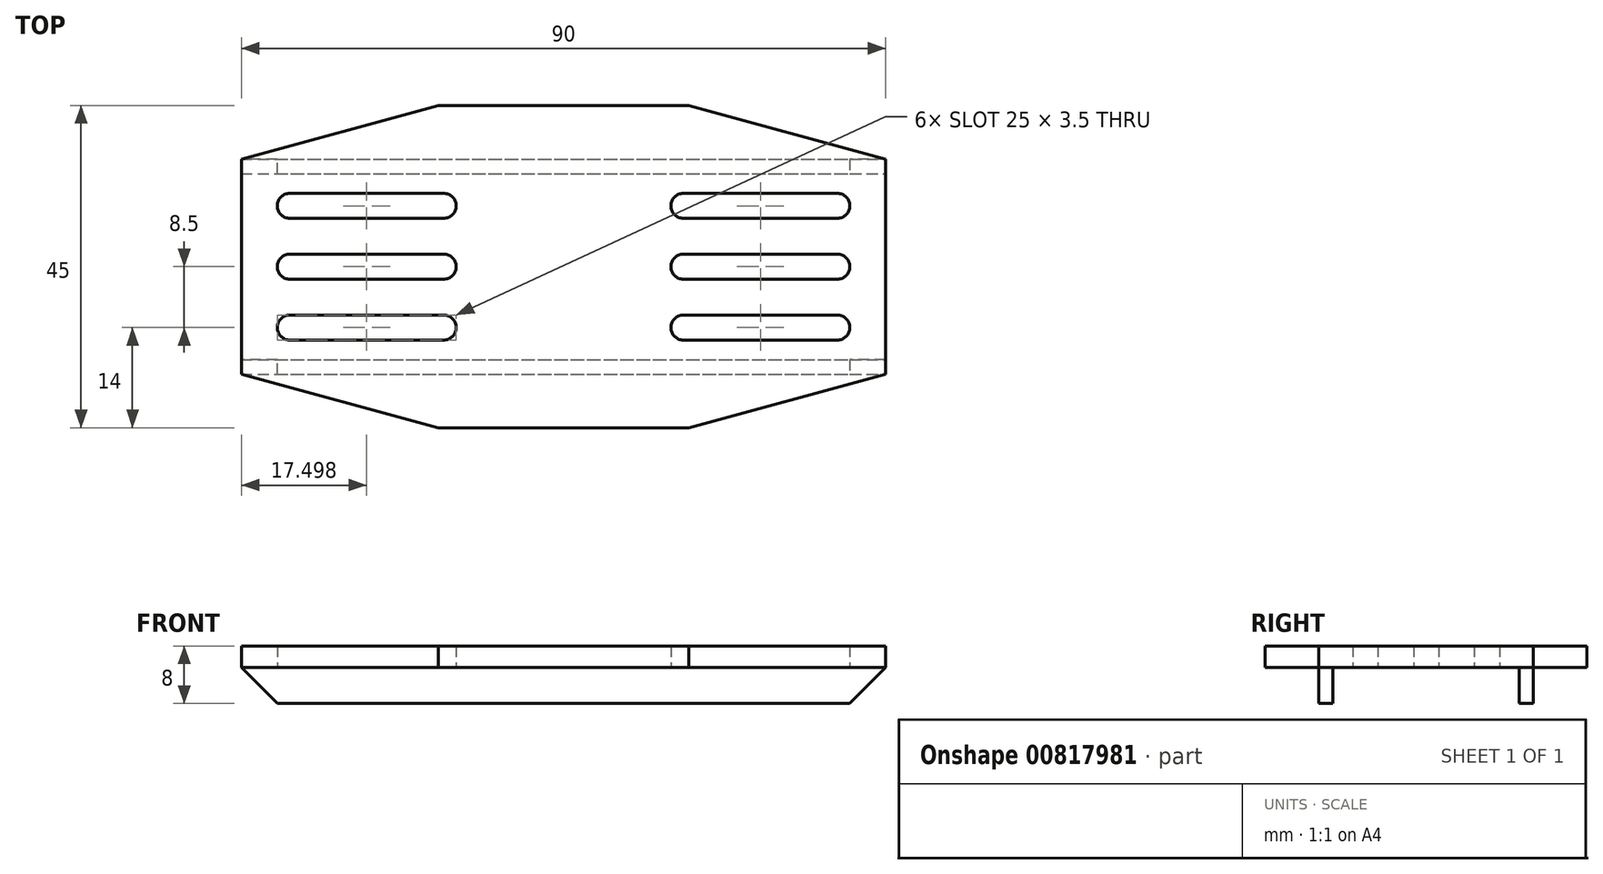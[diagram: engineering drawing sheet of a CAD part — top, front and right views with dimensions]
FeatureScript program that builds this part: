
annotation { "Feature Type Name" : "Feature", "Feature Type Description" : "" }
export const myFeature = defineFeature(function(context is Context, id is Id, definition is map)
    precondition{}
    {
        {
            var Q0;
            Q0=qCreatedBy(makeId("Top.planeOp"),FACE);
            var sketch = newSketch(context, id + "F0", { "sketchPlane" : qUnion([Q0])});
            skLineSegment(sketch, "E0", {"start": v(-65.37, 45) * mm, "end": v(-30.37, 45) * mm});
            skLineSegment(sketch, "E1", {"start": v(-30.37, 45) * mm, "end": v(-2.87, 37.5) * mm});
            skLineSegment(sketch, "E2", {"start": v(-2.87, 37.5) * mm, "end": v(-2.87, 7.5) * mm});
            skLineSegment(sketch, "E3", {"start": v(-2.87, 7.5) * mm, "end": v(-30.37, 0) * mm});
            skLineSegment(sketch, "E4", {"start": v(-30.37, 0) * mm, "end": v(-65.37, 0) * mm});
            skLineSegment(sketch, "E5", {"start": v(-65.37, 0) * mm, "end": v(-92.87, 7.5) * mm});
            skLineSegment(sketch, "E6", {"start": v(-92.87, 7.5) * mm, "end": v(-92.87, 37.5) * mm});
            skLineSegment(sketch, "E7", {"start": v(-92.87, 37.5) * mm, "end": v(-65.37, 45) * mm});
            skLineSegment(sketch, "E8", {"start": v(-92.87, 22.5) * mm, "end": v(-2.87, 22.5) * mm});
            skLineSegment(sketch, "E9", {"start": v(-92.87, 31) * mm, "end": v(-2.87, 31) * mm});
            skLineSegment(sketch, "E10", {"start": v(-92.87, 14) * mm, "end": v(-2.87, 14) * mm});
            skLineSegment(sketch, "E11.bottom", {"start": v(-86.12, 32.75) * mm, "end": v(-64.62, 32.75) * mm});
            skLineSegment(sketch, "E11.top", {"start": v(-86.12, 29.25) * mm, "end": v(-64.62, 29.25) * mm});
            skLineSegment(sketch, "E11.left", {"start": v(-87.87, 31) * mm, "end": v(-87.87, 31) * mm});
            skLineSegment(sketch, "E11.right", {"start": v(-62.87, 31) * mm, "end": v(-62.87, 31) * mm});
            skLineSegment(sketch, "E12.bottom", {"start": v(-86.12, 15.75) * mm, "end": v(-64.62, 15.75) * mm});
            skLineSegment(sketch, "E12.top", {"start": v(-86.12, 12.25) * mm, "end": v(-64.62, 12.25) * mm});
            skLineSegment(sketch, "E12.left", {"start": v(-87.87, 14) * mm, "end": v(-87.87, 14) * mm});
            skLineSegment(sketch, "E12.right", {"start": v(-62.87, 14) * mm, "end": v(-62.87, 14) * mm});
            skLineSegment(sketch, "E13.bottom", {"start": v(-86.12, 24.25) * mm, "end": v(-64.62, 24.25) * mm});
            skLineSegment(sketch, "E13.top", {"start": v(-86.12, 20.75) * mm, "end": v(-64.62, 20.75) * mm});
            skLineSegment(sketch, "E13.left", {"start": v(-87.87, 22.5) * mm, "end": v(-87.87, 22.5) * mm});
            skLineSegment(sketch, "E13.right", {"start": v(-62.87, 22.5) * mm, "end": v(-62.87, 22.5) * mm});
            skLineSegment(sketch, "E14.bottom", {"start": v(-9.62, 32.75) * mm, "end": v(-31.12, 32.75) * mm});
            skLineSegment(sketch, "E14.top", {"start": v(-9.62, 29.25) * mm, "end": v(-31.12, 29.25) * mm});
            skLineSegment(sketch, "E14.left", {"start": v(-7.87, 31) * mm, "end": v(-7.87, 31) * mm});
            skLineSegment(sketch, "E14.right", {"start": v(-32.87, 31) * mm, "end": v(-32.87, 31) * mm});
            skLineSegment(sketch, "E15.bottom", {"start": v(-31.12, 24.25) * mm, "end": v(-9.62, 24.25) * mm});
            skLineSegment(sketch, "E15.top", {"start": v(-31.12, 20.75) * mm, "end": v(-9.62, 20.75) * mm});
            skLineSegment(sketch, "E15.left", {"start": v(-32.87, 22.5) * mm, "end": v(-32.87, 22.5) * mm});
            skLineSegment(sketch, "E15.right", {"start": v(-7.87, 22.5) * mm, "end": v(-7.87, 22.5) * mm});
            skLineSegment(sketch, "E16.bottom", {"start": v(-31.12, 15.75) * mm, "end": v(-9.62, 15.75) * mm});
            skLineSegment(sketch, "E16.top", {"start": v(-31.12, 12.25) * mm, "end": v(-9.62, 12.25) * mm});
            skLineSegment(sketch, "E16.left", {"start": v(-32.87, 14) * mm, "end": v(-32.87, 14) * mm});
            skLineSegment(sketch, "E16.right", {"start": v(-7.87, 14) * mm, "end": v(-7.87, 14) * mm});
            skLineSegment(sketch, "E17", {"start": v(-47.87, 45) * mm, "end": v(-47.87, 0) * mm});
            skLineSegment(sketch, "E18", {"start": v(-92.87, 37.5) * mm, "end": v(-2.87, 37.5) * mm});
            skLineSegment(sketch, "E19", {"start": v(-92.87, 7.5) * mm, "end": v(-2.87, 7.5) * mm});
            skLineSegment(sketch, "E20", {"start": v(-92.87, 9.5) * mm, "end": v(-2.87, 9.5) * mm});
            skLineSegment(sketch, "E21", {"start": v(-92.87, 35.5) * mm, "end": v(-2.87, 35.5) * mm});
            skPoint(sketch, "E22.visualSharp", {"position": v(-62.87, 32.75) * mm});
            skArc(sketch, "E22.filletArc", {"start": v(-62.87, 31) * mm, "mid": v(-63.38, 32.24) * mm, "end": v(-64.62, 32.75) * mm});
            skPoint(sketch, "E23.visualSharp", {"position": v(-62.87, 29.25) * mm});
            skArc(sketch, "E23.filletArc", {"start": v(-64.62, 29.25) * mm, "mid": v(-63.38, 29.76) * mm, "end": v(-62.87, 31) * mm});
            skPoint(sketch, "E24.visualSharp", {"position": v(-62.87, 24.25) * mm});
            skArc(sketch, "E24.filletArc", {"start": v(-62.87, 22.5) * mm, "mid": v(-63.38, 23.74) * mm, "end": v(-64.62, 24.25) * mm});
            skPoint(sketch, "E25.visualSharp", {"position": v(-62.87, 20.75) * mm});
            skArc(sketch, "E25.filletArc", {"start": v(-64.62, 20.75) * mm, "mid": v(-63.38, 21.26) * mm, "end": v(-62.87, 22.5) * mm});
            skPoint(sketch, "E26.visualSharp", {"position": v(-62.87, 15.75) * mm});
            skArc(sketch, "E26.filletArc", {"start": v(-62.87, 14) * mm, "mid": v(-63.38, 15.24) * mm, "end": v(-64.62, 15.75) * mm});
            skPoint(sketch, "E27.visualSharp", {"position": v(-62.87, 12.25) * mm});
            skArc(sketch, "E27.filletArc", {"start": v(-64.62, 12.25) * mm, "mid": v(-63.38, 12.76) * mm, "end": v(-62.87, 14) * mm});
            skPoint(sketch, "E28.visualSharp", {"position": v(-87.87, 12.25) * mm});
            skArc(sketch, "E28.filletArc", {"start": v(-87.87, 14) * mm, "mid": v(-87.36, 12.76) * mm, "end": v(-86.12, 12.25) * mm});
            skPoint(sketch, "E29.visualSharp", {"position": v(-87.87, 15.75) * mm});
            skArc(sketch, "E29.filletArc", {"start": v(-86.12, 15.75) * mm, "mid": v(-87.36, 15.24) * mm, "end": v(-87.87, 14) * mm});
            skPoint(sketch, "E30.visualSharp", {"position": v(-87.87, 20.75) * mm});
            skArc(sketch, "E30.filletArc", {"start": v(-87.87, 22.5) * mm, "mid": v(-87.36, 21.26) * mm, "end": v(-86.12, 20.75) * mm});
            skPoint(sketch, "E31.visualSharp", {"position": v(-87.87, 24.25) * mm});
            skArc(sketch, "E31.filletArc", {"start": v(-86.12, 24.25) * mm, "mid": v(-87.36, 23.74) * mm, "end": v(-87.87, 22.5) * mm});
            skPoint(sketch, "E32.visualSharp", {"position": v(-87.87, 32.75) * mm});
            skArc(sketch, "E32.filletArc", {"start": v(-86.12, 32.75) * mm, "mid": v(-87.36, 32.24) * mm, "end": v(-87.87, 31) * mm});
            skPoint(sketch, "E33.visualSharp", {"position": v(-87.87, 29.25) * mm});
            skArc(sketch, "E33.filletArc", {"start": v(-87.87, 31) * mm, "mid": v(-87.36, 29.76) * mm, "end": v(-86.12, 29.25) * mm});
            skPoint(sketch, "E34.visualSharp", {"position": v(-32.87, 32.75) * mm});
            skArc(sketch, "E34.filletArc", {"start": v(-31.12, 32.75) * mm, "mid": v(-32.36, 32.24) * mm, "end": v(-32.87, 31) * mm});
            skPoint(sketch, "E35.visualSharp", {"position": v(-32.87, 29.25) * mm});
            skArc(sketch, "E35.filletArc", {"start": v(-32.87, 31) * mm, "mid": v(-32.36, 29.76) * mm, "end": v(-31.12, 29.25) * mm});
            skPoint(sketch, "E36.visualSharp", {"position": v(-7.87, 32.75) * mm});
            skArc(sketch, "E36.filletArc", {"start": v(-7.87, 31) * mm, "mid": v(-8.38, 32.24) * mm, "end": v(-9.62, 32.75) * mm});
            skPoint(sketch, "E37.visualSharp", {"position": v(-7.87, 29.25) * mm});
            skArc(sketch, "E37.filletArc", {"start": v(-9.62, 29.25) * mm, "mid": v(-8.38, 29.76) * mm, "end": v(-7.87, 31) * mm});
            skPoint(sketch, "E38.visualSharp", {"position": v(-7.87, 24.25) * mm});
            skArc(sketch, "E38.filletArc", {"start": v(-7.87, 22.5) * mm, "mid": v(-8.38, 23.74) * mm, "end": v(-9.62, 24.25) * mm});
            skPoint(sketch, "E39.visualSharp", {"position": v(-7.87, 20.75) * mm});
            skArc(sketch, "E39.filletArc", {"start": v(-9.62, 20.75) * mm, "mid": v(-8.38, 21.26) * mm, "end": v(-7.87, 22.5) * mm});
            skPoint(sketch, "E40.visualSharp", {"position": v(-32.87, 20.75) * mm});
            skArc(sketch, "E40.filletArc", {"start": v(-32.87, 22.5) * mm, "mid": v(-32.36, 21.26) * mm, "end": v(-31.12, 20.75) * mm});
            skPoint(sketch, "E41.visualSharp", {"position": v(-32.87, 24.25) * mm});
            skArc(sketch, "E41.filletArc", {"start": v(-31.12, 24.25) * mm, "mid": v(-32.36, 23.74) * mm, "end": v(-32.87, 22.5) * mm});
            skPoint(sketch, "E42.visualSharp", {"position": v(-32.87, 15.75) * mm});
            skArc(sketch, "E42.filletArc", {"start": v(-31.12, 15.75) * mm, "mid": v(-32.36, 15.24) * mm, "end": v(-32.87, 14) * mm});
            skPoint(sketch, "E43.visualSharp", {"position": v(-32.87, 12.25) * mm});
            skArc(sketch, "E43.filletArc", {"start": v(-32.87, 14) * mm, "mid": v(-32.36, 12.76) * mm, "end": v(-31.12, 12.25) * mm});
            skPoint(sketch, "E44.visualSharp", {"position": v(-7.87, 15.75) * mm});
            skArc(sketch, "E44.filletArc", {"start": v(-7.87, 14) * mm, "mid": v(-8.38, 15.24) * mm, "end": v(-9.62, 15.75) * mm});
            skPoint(sketch, "E45.visualSharp", {"position": v(-7.87, 12.25) * mm});
            skArc(sketch, "E45.filletArc", {"start": v(-9.62, 12.25) * mm, "mid": v(-8.38, 12.76) * mm, "end": v(-7.87, 14) * mm});
            skSolve(sketch);
        }
        {
            var Q0;
            Q0 = qSketchRegion(id + "F0", true);
            extrude(context, id + "F1", {"entities" : qUnion([Q0]), "depth" : 3 * mm, "offsetDistance" : 25 * mm});
        }
        {
            var Q0;
            {var subQ0=sQuery(id+"F0.wireOp",EDGE,"E18");var subQ5=sQuery(id+"F0.wireOp",EDGE,"E17");var subQ6=makeQuery(id+"F0.imprint","INTERSECT",VERTEX,{"derivedFrom":[subQ5,subQ0]});Q0=makeQuery(id+"F0.imprint","IMPRINT",FACE,{"disambiguationData":[TD([[makeQuery(id+"F0.imprint","IMPRINT",EDGE,{"disambiguationData":[TD([[subQ6,-1.0]])],"derivedFrom":subQ5}),1.0]])]});}
            var Q1;
            {var subQ0=sQuery(id+"F0.wireOp",EDGE,"E18");var subQ5=sQuery(id+"F0.wireOp",EDGE,"E17");var subQ6=makeQuery(id+"F0.imprint","INTERSECT",VERTEX,{"derivedFrom":[subQ5,subQ0]});Q1=makeQuery(id+"F0.imprint","IMPRINT",FACE,{"disambiguationData":[TD([[makeQuery(id+"F0.imprint","IMPRINT",EDGE,{"disambiguationData":[TD([[subQ6,-1.0]])],"derivedFrom":subQ5}),-1.0]])]});}
            var Q2;
            {var subQ3=sQuery(id+"F0.wireOp",EDGE,"E20");var subQ5=sQuery(id+"F0.wireOp",EDGE,"E17");var subQ6=makeQuery(id+"F0.imprint","INTERSECT",VERTEX,{"derivedFrom":[subQ5,subQ3]});Q2=makeQuery(id+"F0.imprint","IMPRINT",FACE,{"disambiguationData":[TD([[makeQuery(id+"F0.imprint","IMPRINT",EDGE,{"disambiguationData":[TD([[subQ6,-1.0]])],"derivedFrom":subQ5}),1.0]])]});}
            var Q3;
            {var subQ3=sQuery(id+"F0.wireOp",EDGE,"E20");var subQ5=sQuery(id+"F0.wireOp",EDGE,"E17");var subQ6=makeQuery(id+"F0.imprint","INTERSECT",VERTEX,{"derivedFrom":[subQ5,subQ3]});Q3=makeQuery(id+"F0.imprint","IMPRINT",FACE,{"disambiguationData":[TD([[makeQuery(id+"F0.imprint","IMPRINT",EDGE,{"disambiguationData":[TD([[subQ6,-1.0]])],"derivedFrom":subQ5}),-1.0]])]});}
            extrude(context, id + "F2", {"entities" : qUnion([Q0, Q1, Q2, Q3]), "operationType" : NewBodyOperationType.ADD, "oppositeDirection" : true, "depth" : 5 * mm, "offsetDistance" : 25 * mm});
        }
        {
            var Q0;
            {var subQ0=sQuery(id+"F0.wireOp",EDGE,"E6");Q0=makeQuery(id+"F2.opExtrude","CAP_EDGE",EDGE,{"disambiguationData":[OSD([subQ0]),TDD([makeQuery(id+"F0.imprint","IMPRINT",EDGE,{"disambiguationData":[TD([[makeQuery(id+"F0.imprint","INTERSECT",VERTEX,{"derivedFrom":[subQ0,sQuery(id+"F0.wireOp",EDGE,"E21")]}),-1.0]])],"derivedFrom":subQ0})])],"isStart":false});}
            var Q1;
            {var subQ0=sQuery(id+"F0.wireOp",EDGE,"E6");Q1=makeQuery(id+"F2.opExtrude","CAP_EDGE",EDGE,{"disambiguationData":[OSD([subQ0]),TDD([makeQuery(id+"F0.imprint","IMPRINT",EDGE,{"disambiguationData":[TD([[makeQuery(id+"F0.imprint","INTERSECT",VERTEX,{"derivedFrom":[subQ0,sQuery(id+"F0.wireOp",EDGE,"E20")]}),1.0]])],"derivedFrom":subQ0})])],"isStart":false});}
            var Q2;
            {var subQ0=sQuery(id+"F0.wireOp",EDGE,"E2");Q2=makeQuery(id+"F2.opExtrude","CAP_EDGE",EDGE,{"disambiguationData":[OSD([subQ0]),TDD([makeQuery(id+"F0.imprint","IMPRINT",EDGE,{"disambiguationData":[TD([[makeQuery(id+"F0.imprint","INTERSECT",VERTEX,{"derivedFrom":[subQ0,sQuery(id+"F0.wireOp",EDGE,"E20")]}),-1.0]])],"derivedFrom":subQ0})])],"isStart":false});}
            var Q3;
            {var subQ0=sQuery(id+"F0.wireOp",EDGE,"E2");Q3=makeQuery(id+"F2.opExtrude","CAP_EDGE",EDGE,{"disambiguationData":[OSD([subQ0]),TDD([makeQuery(id+"F0.imprint","IMPRINT",EDGE,{"disambiguationData":[TD([[makeQuery(id+"F0.imprint","INTERSECT",VERTEX,{"derivedFrom":[subQ0,sQuery(id+"F0.wireOp",EDGE,"E21")]}),1.0]])],"derivedFrom":subQ0})])],"isStart":false});}
            chamfer(context, id + "F3", {"entities" : qUnion([Q0, Q1, Q2, Q3]), "width" : 5 * mm, "tangentPropagation" : true});
        }
    });
